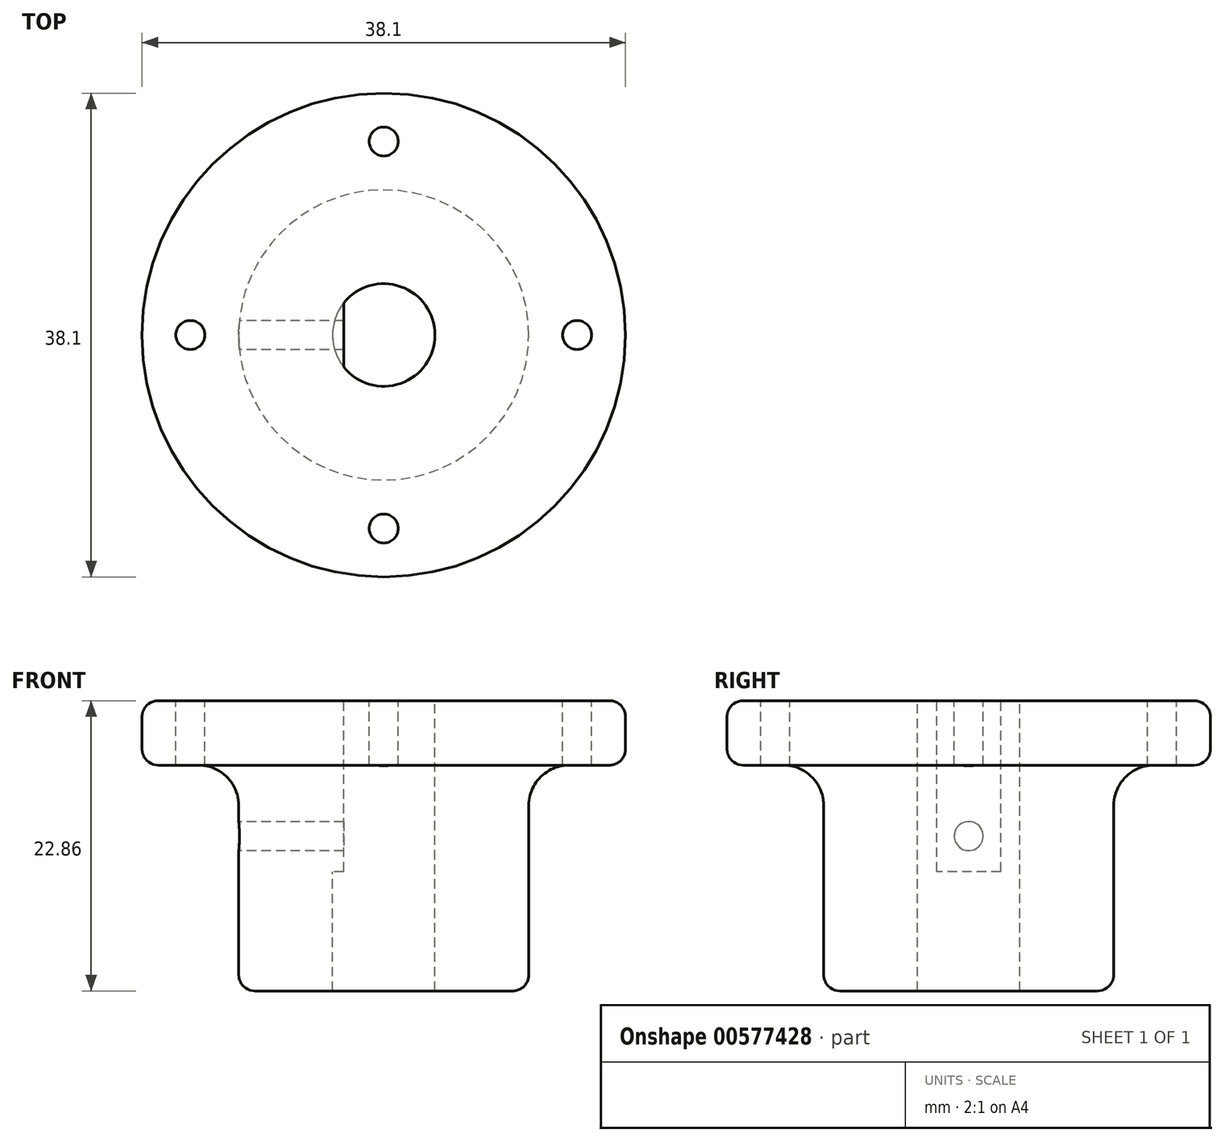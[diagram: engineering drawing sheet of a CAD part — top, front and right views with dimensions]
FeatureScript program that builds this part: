
annotation { "Feature Type Name" : "Feature", "Feature Type Description" : "" }
export const myFeature = defineFeature(function(context is Context, id is Id, definition is map)
    precondition{}
    {
        {
            var Q0;
            Q0=qCreatedBy(makeId("Top.planeOp"),FACE);
            var sketch = newSketch(context, id + "F0", { "sketchPlane" : qUnion([Q0])});
            skCircle(sketch, "E0", {"center": v(0, 0) * mm, "radius": 4.04 * mm});
            skSolve(sketch);
        }
        {
            var Q0;
            Q0=makeQuery(id+"F0.imprint","IMPRINT",FACE,{"disambiguationData":[TD([[makeQuery(id+"F0.imprint","IMPRINT",EDGE,{"derivedFrom":sQuery(id+"F0.wireOp",EDGE,"E0")}),1.0]])]});
            var sketch = newSketch(context, id + "F1", { "sketchPlane" : qUnion([Q0])});
            skCircle(sketch, "E1", {"center": v(0, 0) * mm, "radius": 19.05 * mm});
            skSolve(sketch);
        }
        {
            var Q0;
            Q0=qCreatedBy(makeId("Top.planeOp"),FACE);
            var sketch = newSketch(context, id + "F2", { "sketchPlane" : qUnion([Q0])});
            skCircle(sketch, "E2", {"center": v(0, 0) * mm, "radius": 11.43 * mm});
            skSolve(sketch);
        }
        {
            var Q0;
            Q0=qCreatedBy(makeId("Top.planeOp"),FACE);
            var sketch = newSketch(context, id + "F3", { "sketchPlane" : qUnion([Q0])});
            skArc(sketch, "E3", {"start": v(-3.15, 2.53) * mm, "mid": v(-4.04, 0) * mm, "end": v(-3.15, -2.53) * mm});
            skLineSegment(sketch, "E4", {"start": v(-3.15, 2.57) * mm, "end": v(-3.15, -2.57) * mm});
            skSolve(sketch);
        }
        {
            var Q0;
            Q0=makeQuery(id+"F2.imprint","IMPRINT",FACE,{"disambiguationData":[TD([[makeQuery(id+"F2.imprint","IMPRINT",EDGE,{"derivedFrom":sQuery(id+"F2.wireOp",EDGE,"E2")}),1.0]])]});
            extrude(context, id + "F4", {"entities" : qUnion([Q0]), "oppositeDirection" : true, "depth" : 22.86 * mm, "offsetDistance" : 25.4 * mm});
        }
        {
            var Q0;
            Q0=makeQuery(id+"F1.imprint","IMPRINT",FACE,{"disambiguationData":[TD([[makeQuery(id+"F1.imprint","IMPRINT",EDGE,{"derivedFrom":sQuery(id+"F1.wireOp",EDGE,"E1")}),1.0]])]});
            var Q1;
            Q1=sQuery(id+"F1.wireOp",EDGE,"E1");
            extrude(context, id + "F5", {"entities" : qUnion([Q0]), "operationType" : NewBodyOperationType.ADD, "surfaceEntities" : qUnion([Q1]), "oppositeDirection" : true, "depth" : 5.08 * mm, "offsetDistance" : 25.4 * mm});
        }
        {
            var Q0;
            Q0 = qSketchRegion(id + "F0", true);
            extrude(context, id + "F6", {"entities" : qUnion([Q0]), "operationType" : NewBodyOperationType.REMOVE, "oppositeDirection" : true, "depth" : 22.86 * mm, "offsetDistance" : 25.4 * mm});
        }
        {
            var Q0;
            Q0 = qSketchRegion(id + "F3", true);
            extrude(context, id + "F7", {"entities" : qUnion([Q0]), "operationType" : NewBodyOperationType.ADD, "oppositeDirection" : true, "depth" : 13.46 * mm, "offsetDistance" : 25.4 * mm});
        }
        {
            var Q0;
            Q0=qCreatedBy(makeId("Right.planeOp"),FACE);
            cPlane(context, id + "F8", {"entities" : qUnion([Q0]), "cplaneType" : CPlaneType.OFFSET, "offset" : 11.43 * mm, "oppositeDirection" : true, "width" : 152.4 * mm, "height" : 152.4 * mm});
        }
        {
            var Q0;
            Q0=qCreatedBy(id+"F8.planeOp",FACE);
            var sketch = newSketch(context, id + "F9", { "sketchPlane" : qUnion([Q0])});
            skCircle(sketch, "E5", {"center": v(0, -10.67) * mm, "radius": 1.14 * mm});
            skSolve(sketch);
        }
        {
            var Q0;
            Q0=makeQuery(id+"F9.imprint","IMPRINT",FACE,{"disambiguationData":[TD([[makeQuery(id+"F9.imprint","IMPRINT",EDGE,{"derivedFrom":sQuery(id+"F9.wireOp",EDGE,"E5")}),1.0]])]});
            extrude(context, id + "F10", {"entities" : qUnion([Q0]), "operationType" : NewBodyOperationType.REMOVE, "depth" : 11.43 * mm, "offsetDistance" : 25.4 * mm});
        }
        {
            var Q0;
            Q0=makeQuery(id+"F5.boolean.opBoolean","INTERSECT",EDGE,{"derivedFrom":[makeQuery(id+"F4.opExtrude","SWEPT_FACE",FACE,{"disambiguationData":[OSD([sQuery(id+"F2.wireOp",EDGE,"E2")])]}),makeQuery(id+"F5.opExtrude","CAP_FACE",FACE,{"disambiguationData":[OSD([sQuery(id+"F0.wireOp",EDGE,"E0"),sQuery(id+"F1.wireOp",EDGE,"E1")])],"isStart":false})]});
            fillet(context, id + "F11", {"entities" : qUnion([Q0]), "radius" : 3.17 * mm, "tangentPropagation" : true, "allowEdgeOverflow" : false});
        }
        {
            var Q0;
            Q0=makeQuery(id+"F4.opExtrude","CAP_EDGE",EDGE,{"disambiguationData":[OSD([sQuery(id+"F2.wireOp",EDGE,"E2")])],"isStart":false});
            var Q1;
            Q1=makeQuery(id+"F5.opExtrude","CAP_EDGE",EDGE,{"disambiguationData":[OSD([sQuery(id+"F1.wireOp",EDGE,"E1")])],"isStart":false});
            var Q2;
            Q2=makeQuery(id+"F6.boolean.opBoolean","COPY",EDGE,{"derivedFrom":makeQuery(id+"F6.opExtrude","CAP_EDGE",EDGE,{"disambiguationData":[OSD([sQuery(id+"F0.wireOp",EDGE,"E0")])],"isStart":false})});
            var Q3;
            Q3=makeQuery(id+"F5.opExtrude","CAP_EDGE",EDGE,{"disambiguationData":[OSD([sQuery(id+"F1.wireOp",EDGE,"E1")])],"isStart":true});
            fillet(context, id + "F12", {"entities" : qUnion([Q0, Q1, Q2, Q3]), "radius" : 1.27 * mm, "tangentPropagation" : true, "allowEdgeOverflow" : false});
        }
        {
            var Q0;
            Q0=qCreatedBy(makeId("Top.planeOp"),FACE);
            var sketch = newSketch(context, id + "F13", { "sketchPlane" : qUnion([Q0])});
            skCircle(sketch, "E6", {"center": v(0, 0) * mm, "radius": 15.24 * mm, "construction": true});
            skCircle(sketch, "E7", {"center": v(15.24, 0) * mm, "radius": 1.14 * mm});
            skCircle(sketch, "E8", {"center": v(-15.24, 0) * mm, "radius": 1.14 * mm});
            skCircle(sketch, "E9", {"center": v(0, -15.24) * mm, "radius": 1.14 * mm});
            skCircle(sketch, "E10", {"center": v(0, 15.24) * mm, "radius": 1.14 * mm});
            skSolve(sketch);
        }
        {
            var Q0;
            Q0=makeQuery(id+"F13.imprint","IMPRINT",FACE,{"disambiguationData":[TD([[makeQuery(id+"F13.imprint","IMPRINT",EDGE,{"derivedFrom":sQuery(id+"F13.wireOp",EDGE,"E7")}),1.0]])]});
            var Q1;
            Q1=makeQuery(id+"F13.imprint","IMPRINT",FACE,{"disambiguationData":[TD([[makeQuery(id+"F13.imprint","IMPRINT",EDGE,{"derivedFrom":sQuery(id+"F13.wireOp",EDGE,"E10")}),1.0]])]});
            var Q2;
            Q2=makeQuery(id+"F13.imprint","IMPRINT",FACE,{"disambiguationData":[TD([[makeQuery(id+"F13.imprint","IMPRINT",EDGE,{"derivedFrom":sQuery(id+"F13.wireOp",EDGE,"E9")}),1.0]])]});
            var Q3;
            Q3=makeQuery(id+"F13.imprint","IMPRINT",FACE,{"disambiguationData":[TD([[makeQuery(id+"F13.imprint","IMPRINT",EDGE,{"derivedFrom":sQuery(id+"F13.wireOp",EDGE,"E8")}),1.0]])]});
            var Q4;
            Q4=sQuery(id+"F13.wireOp",EDGE,"E6");
            var Q5;
            Q5=sQuery(id+"F13.wireOp",EDGE,"E7");
            var Q6;
            Q6=sQuery(id+"F13.wireOp",EDGE,"E9");
            var Q7;
            Q7=sQuery(id+"F13.wireOp",EDGE,"E8");
            var Q8;
            Q8=sQuery(id+"F13.wireOp",EDGE,"E10");
            extrude(context, id + "F14", {"entities" : qUnion([Q0, Q1, Q2, Q3]), "operationType" : NewBodyOperationType.REMOVE, "surfaceEntities" : qUnion([Q4, Q5, Q6, Q7, Q8]), "endBound" : BoundingType.UP_TO_NEXT, "oppositeDirection" : true, "depth" : 25.4 * mm, "offsetDistance" : 25.4 * mm});
        }
    });
